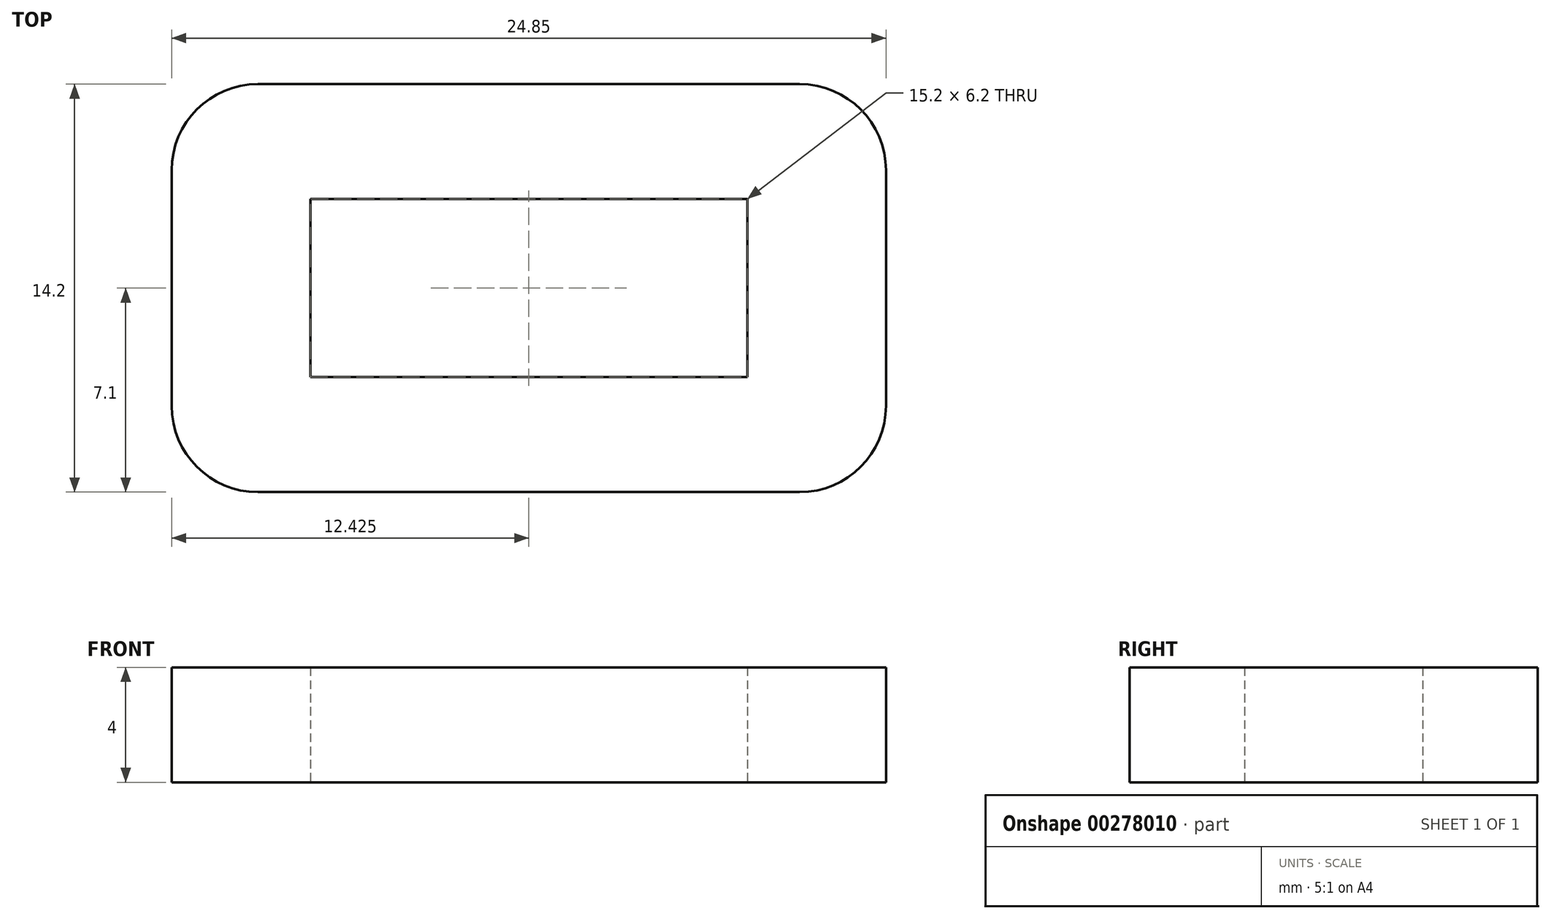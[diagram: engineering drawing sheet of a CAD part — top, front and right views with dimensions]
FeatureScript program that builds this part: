
annotation { "Feature Type Name" : "Feature", "Feature Type Description" : "" }
export const myFeature = defineFeature(function(context is Context, id is Id, definition is map)
    precondition{}
    {
        {
            var Q0;
            Q0=qCreatedBy(makeId("Top.planeOp"),FACE);
            var sketch = newSketch(context, id + "F0", { "sketchPlane" : qUnion([Q0])});
            skLineSegment(sketch, "E0", {"start": v(3, 0) * mm, "end": v(21.85, 0) * mm});
            skLineSegment(sketch, "E1", {"start": v(24.85, -3) * mm, "end": v(24.85, -11.2) * mm});
            skLineSegment(sketch, "E2", {"start": v(21.85, -14.2) * mm, "end": v(3, -14.2) * mm});
            skLineSegment(sketch, "E3", {"start": v(0, -11.2) * mm, "end": v(0, -3) * mm});
            skPoint(sketch, "E4.visualSharp", {"position": v(0, 0) * mm});
            skArc(sketch, "E4.filletArc", {"start": v(3, 0) * mm, "mid": v(0.88, -0.88) * mm, "end": v(0, -3) * mm});
            skPoint(sketch, "E5.visualSharp", {"position": v(24.85, 0) * mm});
            skArc(sketch, "E5.filletArc", {"start": v(24.85, -3) * mm, "mid": v(23.97, -0.88) * mm, "end": v(21.85, 0) * mm});
            skPoint(sketch, "E6.visualSharp", {"position": v(24.85, -14.2) * mm});
            skArc(sketch, "E6.filletArc", {"start": v(21.85, -14.2) * mm, "mid": v(23.97, -13.32) * mm, "end": v(24.85, -11.2) * mm});
            skPoint(sketch, "E7.visualSharp", {"position": v(0, -14.2) * mm});
            skArc(sketch, "E7.filletArc", {"start": v(0, -11.2) * mm, "mid": v(0.88, -13.32) * mm, "end": v(3, -14.2) * mm});
            skLineSegment(sketch, "E8.bottom", {"start": v(4.83, -4) * mm, "end": v(20.03, -4) * mm});
            skLineSegment(sketch, "E8.top", {"start": v(4.83, -10.2) * mm, "end": v(20.03, -10.2) * mm});
            skLineSegment(sketch, "E8.left", {"start": v(4.83, -4) * mm, "end": v(4.83, -10.2) * mm});
            skLineSegment(sketch, "E8.right", {"start": v(20.03, -4) * mm, "end": v(20.03, -10.2) * mm});
            skPoint(sketch, "E9", {"position": v(12.43, -4) * mm});
            skPoint(sketch, "E10", {"position": v(12.43, 0) * mm});
            skPoint(sketch, "E11", {"position": v(24.85, -7.1) * mm});
            skPoint(sketch, "E12", {"position": v(20.03, -7.1) * mm});
            skSolve(sketch);
        }
        {
            var Q0;
            Q0 = qSketchRegion(id + "F0", true);
            extrude(context, id + "F1", {"entities" : qUnion([Q0]), "depth" : 4 * mm});
        }
    });
